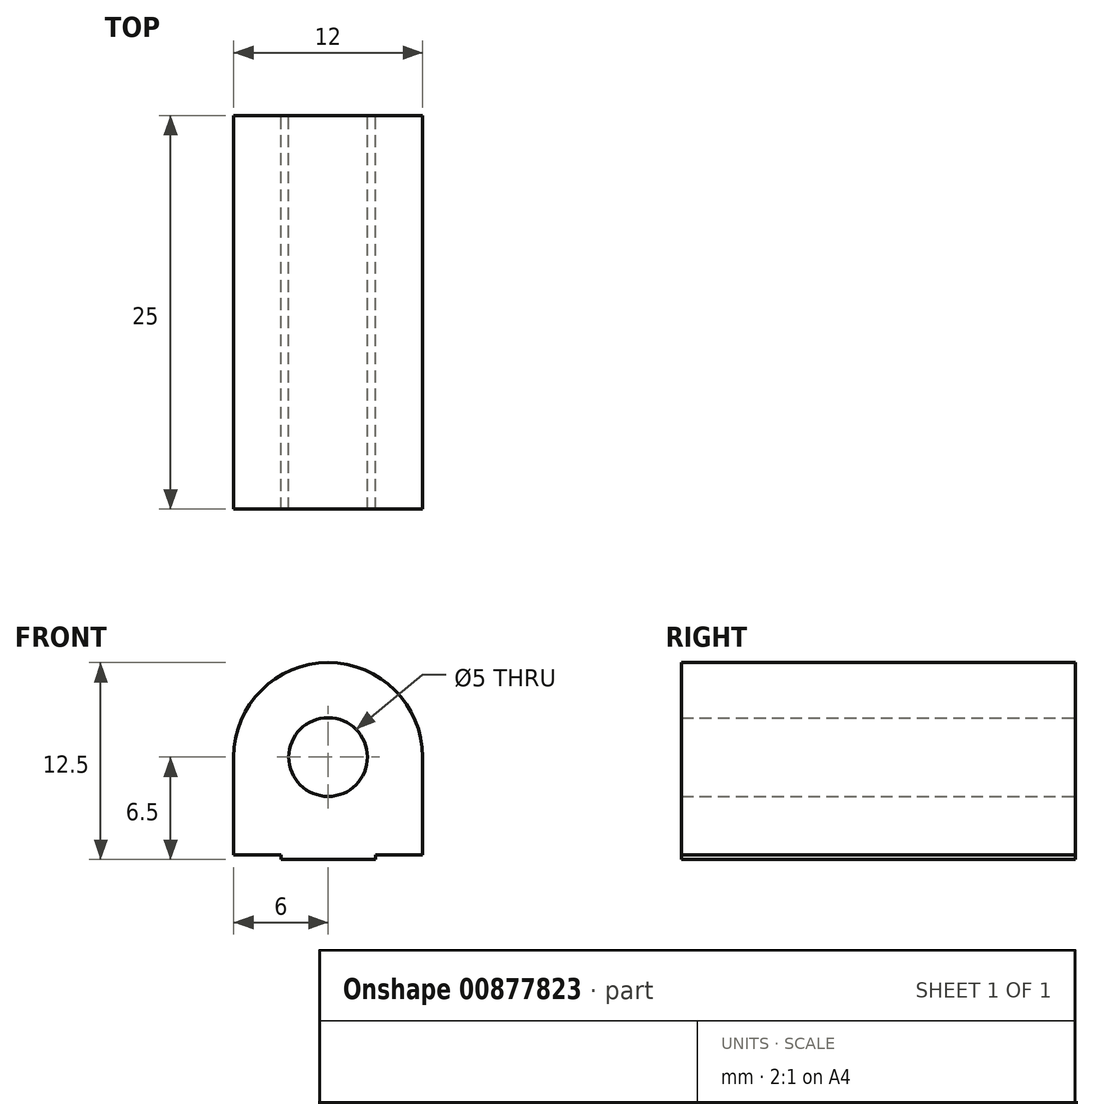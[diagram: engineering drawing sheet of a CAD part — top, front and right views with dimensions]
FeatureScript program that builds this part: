
annotation { "Feature Type Name" : "Feature", "Feature Type Description" : "" }
export const myFeature = defineFeature(function(context is Context, id is Id, definition is map)
    precondition{}
    {
        {
            var Q0;
            Q0=qCreatedBy(makeId("Front.planeOp"),FACE);
            var sketch = newSketch(context, id + "F0", { "sketchPlane" : qUnion([Q0])});
            skCircle(sketch, "E0", {"center": v(0, 0) * mm, "radius": 2.5 * mm});
            skArc(sketch, "E1", {"start": v(6, 0) * mm, "mid": v(0, 6) * mm, "end": v(-6, 0) * mm});
            skLineSegment(sketch, "E2", {"start": v(-3, -6.5) * mm, "end": v(3, -6.5) * mm});
            skLineSegment(sketch, "E3", {"start": v(3, -6.5) * mm, "end": v(3, -6.2) * mm});
            skLineSegment(sketch, "E4", {"start": v(3, -6.2) * mm, "end": v(6, -6.2) * mm});
            skLineSegment(sketch, "E5", {"start": v(-3, -6.5) * mm, "end": v(-3, -6.2) * mm});
            skLineSegment(sketch, "E6", {"start": v(-3, -6.2) * mm, "end": v(-6, -6.2) * mm});
            skLineSegment(sketch, "E7", {"start": v(6, -6.2) * mm, "end": v(6, 0) * mm});
            skLineSegment(sketch, "E8", {"start": v(-6, 0) * mm, "end": v(-6, -6.2) * mm});
            skSolve(sketch);
        }
        {
            var Q0;
            Q0 = qSketchRegion(id + "F0", true);
            extrude(context, id + "F1", {"entities" : qUnion([Q0]), "depth" : 25 * mm, "offsetDistance" : 25 * mm});
        }
    });
